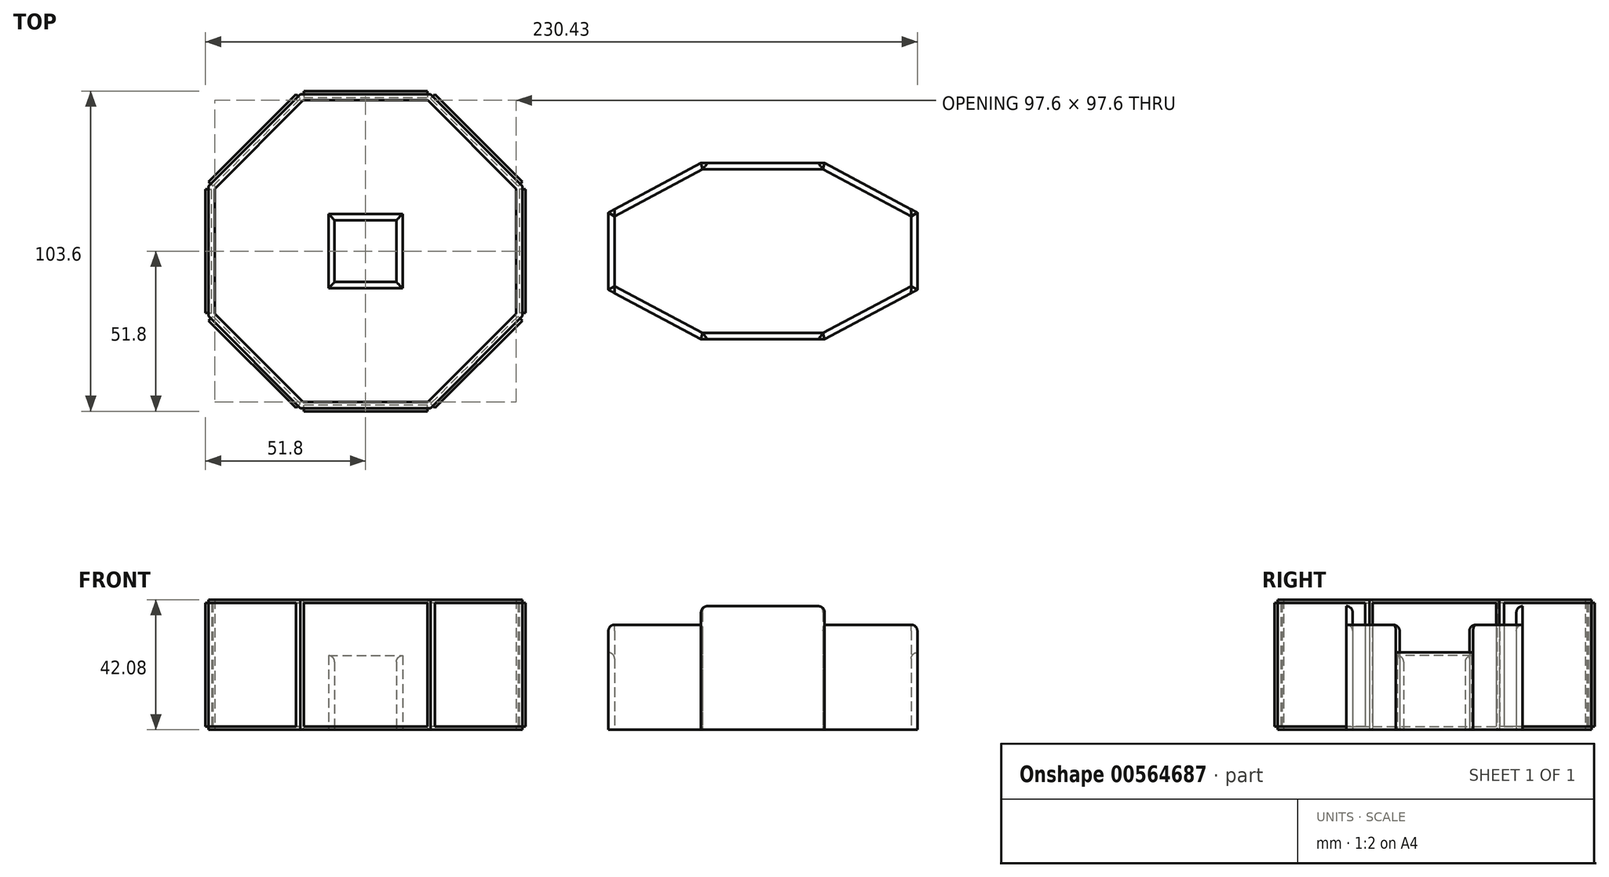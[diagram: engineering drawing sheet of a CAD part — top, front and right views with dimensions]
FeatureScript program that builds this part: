
annotation { "Feature Type Name" : "Feature", "Feature Type Description" : "" }
export const myFeature = defineFeature(function(context is Context, id is Id, definition is map)
    precondition{}
    {
        {
            var Q0;
            Q0=qCreatedBy(makeId("Top.planeOp"),FACE);
            var sketch = newSketch(context, id + "F0", { "sketchPlane" : qUnion([Q0])});
            skCircle(sketch, "E0.cCircle", {"center": v(0, 0) * mm, "radius": 50.8 * mm, "construction": true});
            skLineSegment(sketch, "E0.0", {"start": v(-50.8, -21.04) * mm, "end": v(-50.8, 21.04) * mm});
            skLineSegment(sketch, "E0.1", {"start": v(-50.8, 21.04) * mm, "end": v(-21.04, 50.8) * mm});
            skLineSegment(sketch, "E0.2", {"start": v(-21.04, 50.8) * mm, "end": v(21.04, 50.8) * mm});
            skLineSegment(sketch, "E0.3", {"start": v(21.04, 50.8) * mm, "end": v(50.8, 21.04) * mm});
            skLineSegment(sketch, "E0.4", {"start": v(50.8, 21.04) * mm, "end": v(50.8, -21.04) * mm});
            skLineSegment(sketch, "E0.5", {"start": v(50.8, -21.04) * mm, "end": v(21.04, -50.8) * mm});
            skLineSegment(sketch, "E0.6", {"start": v(21.04, -50.8) * mm, "end": v(-21.04, -50.8) * mm});
            skLineSegment(sketch, "E0.7", {"start": v(-21.04, -50.8) * mm, "end": v(-50.8, -21.04) * mm});
            skPoint(sketch, "E0.0.midPoint", {"position": v(-50.8, 0) * mm});
            skLineSegment(sketch, "E1.0", {"start": v(-48.8, -20.21) * mm, "end": v(-48.8, 20.21) * mm});
            skLineSegment(sketch, "E1.1", {"start": v(-20.21, -48.8) * mm, "end": v(-48.8, -20.21) * mm});
            skLineSegment(sketch, "E1.2", {"start": v(-48.8, 20.21) * mm, "end": v(-20.21, 48.8) * mm});
            skLineSegment(sketch, "E1.3", {"start": v(20.21, -48.8) * mm, "end": v(-20.21, -48.8) * mm});
            skLineSegment(sketch, "E1.4", {"start": v(-20.21, 48.8) * mm, "end": v(20.21, 48.8) * mm});
            skLineSegment(sketch, "E1.5", {"start": v(20.21, 48.8) * mm, "end": v(48.8, 20.21) * mm});
            skLineSegment(sketch, "E1.6", {"start": v(48.8, 20.21) * mm, "end": v(48.8, -20.21) * mm});
            skLineSegment(sketch, "E1.7", {"start": v(48.8, -20.21) * mm, "end": v(20.21, -48.8) * mm});
            skSolve(sketch);
        }
        {
            var Q0;
            Q0 = qSketchRegion(id + "F0", true);
            extrude(context, id + "F1", {"entities" : qUnion([Q0]), "depth" : 42.08 * mm, "offsetDistance" : 25.4 * mm});
        }
        {
            var Q0;
            Q0=qCreatedBy(makeId("Top.planeOp"),FACE);
            var sketch = newSketch(context, id + "F2", { "sketchPlane" : qUnion([Q0])});
            skCircle(sketch, "E2.cCircle", {"center": v(0, 0) * mm, "radius": 12 * mm, "construction": true});
            skLineSegment(sketch, "E2.0", {"start": v(12, 12) * mm, "end": v(12, -12) * mm});
            skLineSegment(sketch, "E2.1", {"start": v(12, -12) * mm, "end": v(-12, -12) * mm});
            skLineSegment(sketch, "E2.2", {"start": v(-12, -12) * mm, "end": v(-12, 12) * mm});
            skLineSegment(sketch, "E2.3", {"start": v(-12, 12) * mm, "end": v(12, 12) * mm});
            skPoint(sketch, "E2.0.midPoint", {"position": v(12, 0) * mm});
            skLineSegment(sketch, "E3.0", {"start": v(10, -10) * mm, "end": v(-10, -10) * mm});
            skLineSegment(sketch, "E3.1", {"start": v(10, 10) * mm, "end": v(10, -10) * mm});
            skLineSegment(sketch, "E3.2", {"start": v(-10, 10) * mm, "end": v(10, 10) * mm});
            skLineSegment(sketch, "E3.3", {"start": v(-10, -10) * mm, "end": v(-10, 10) * mm});
            skSolve(sketch);
        }
        {
            var Q0;
            Q0 = qSketchRegion(id + "F2", true);
            extrude(context, id + "F3", {"entities" : qUnion([Q0]), "depth" : 24 * mm, "offsetDistance" : 25.4 * mm});
        }
        {
            var Q0;
            Q0=makeQuery(id+"F1.opExtrude","SWEPT_FACE",FACE,{"disambiguationData":[OSD([sQuery(id+"F0.wireOp",EDGE,"E0.2")])]});
            var sketch = newSketch(context, id + "F4", { "sketchPlane" : qUnion([Q0])});
            skLineSegment(sketch, "E4.bottom", {"start": v(20, 41.04) * mm, "end": v(-20, 41.04) * mm});
            skLineSegment(sketch, "E4.top", {"start": v(20, 1.04) * mm, "end": v(-20, 1.04) * mm});
            skLineSegment(sketch, "E4.left", {"start": v(20, 41.04) * mm, "end": v(20, 1.04) * mm});
            skLineSegment(sketch, "E4.right", {"start": v(-20, 41.04) * mm, "end": v(-20, 1.04) * mm});
            skPoint(sketch, "E4.middle", {"position": v(0, 21.04) * mm});
            skPoint(sketch, "E4.middle.positionSnap0", {"position": v(-21.04, 21.04) * mm});
            skPoint(sketch, "E4.middle.positionSnap1", {"position": v(0, 0) * mm});
            skPoint(sketch, "E4.centerSnap0", {"position": v(-21.04, 21.04) * mm});
            skPoint(sketch, "E4.centerSnap1", {"position": v(0, 0) * mm});
            skSolve(sketch);
        }
        {
            var Q0;
            Q0 = qSketchRegion(id + "F4", true);
            extrude(context, id + "F5", {"entities" : qUnion([Q0]), "endBound" : BoundingType.SYMMETRIC, "depth" : 2 * mm, "offsetDistance" : 25.4 * mm});
        }
        {
            var Q0;
            Q0=qCreatedBy(makeId("Front.planeOp"),FACE);
            var sketch = newSketch(context, id + "F6", { "sketchPlane" : qUnion([Q0])});
            skLineSegment(sketch, "E5", {"start": v(0, 0) * mm, "end": v(0, 64.3) * mm});
            skSolve(sketch);
        }
        {
            var Q0;
            Q0=makeQuery(id+"F5.opExtrude","SWEPT_BODY",BODY,{"disambiguationData":[OSD([sQuery(id+"F4.wireOp",EDGE,"E4.bottom"),sQuery(id+"F4.wireOp",EDGE,"E4.top"),sQuery(id+"F4.wireOp",EDGE,"E4.left"),sQuery(id+"F4.wireOp",EDGE,"E4.right")])]});
            var Q1;
            Q1=sQuery(id+"F6.wireOp",EDGE,"E5");
            circularPattern(context, id + "F7", {"entities" : qUnion([Q0]), "axis" : qUnion([Q1]), "angle" : 360 * degree, "instanceCount" : 8, "equalSpace" : true});
        }
        {
            var Q0;
            Q0=qCreatedBy(makeId("Top.planeOp"),FACE);
            var sketch = newSketch(context, id + "F8", { "sketchPlane" : qUnion([Q0])});
            skLineSegment(sketch, "E6", {"start": v(78.63, 0) * mm, "end": v(78.63, 12.5) * mm});
            skLineSegment(sketch, "E7", {"start": v(78.63, 12.5) * mm, "end": v(108.63, 28.5) * mm});
            skLineSegment(sketch, "E8", {"start": v(108.63, 28.5) * mm, "end": v(148.63, 28.5) * mm});
            skLineSegment(sketch, "E9", {"start": v(148.63, 28.5) * mm, "end": v(178.63, 12.5) * mm});
            skLineSegment(sketch, "E10", {"start": v(178.63, 12.5) * mm, "end": v(178.63, 0) * mm});
            skLineSegment(sketch, "E11", {"start": v(78.63, 0) * mm, "end": v(178.63, 0) * mm, "construction": true});
            skLineSegment(sketch, "E12.MirrorCS", {"start": v(178.63, -12.5) * mm, "end": v(178.63, 0) * mm});
            skLineSegment(sketch, "E13.MirrorCS", {"start": v(148.63, -28.5) * mm, "end": v(178.63, -12.5) * mm});
            skLineSegment(sketch, "E14.MirrorCS", {"start": v(108.63, -28.5) * mm, "end": v(148.63, -28.5) * mm});
            skLineSegment(sketch, "E15.MirrorCS", {"start": v(78.63, 0) * mm, "end": v(78.63, -12.5) * mm});
            skLineSegment(sketch, "E16.MirrorCS", {"start": v(78.63, -12.5) * mm, "end": v(108.63, -28.5) * mm});
            skLineSegment(sketch, "E17.0", {"start": v(80.63, 11.3) * mm, "end": v(109.13, 26.5) * mm});
            skLineSegment(sketch, "E17.1", {"start": v(80.63, 0) * mm, "end": v(80.63, 11.3) * mm});
            skLineSegment(sketch, "E17.2", {"start": v(109.13, 26.5) * mm, "end": v(148.13, 26.5) * mm});
            skLineSegment(sketch, "E17.3", {"start": v(80.63, 0) * mm, "end": v(80.63, -11.3) * mm});
            skLineSegment(sketch, "E17.4", {"start": v(80.63, -11.3) * mm, "end": v(109.13, -26.5) * mm});
            skLineSegment(sketch, "E17.5", {"start": v(109.13, -26.5) * mm, "end": v(148.13, -26.5) * mm});
            skLineSegment(sketch, "E17.6", {"start": v(148.13, 26.5) * mm, "end": v(176.63, 11.3) * mm});
            skLineSegment(sketch, "E17.7", {"start": v(176.63, 11.3) * mm, "end": v(176.63, 0) * mm});
            skLineSegment(sketch, "E17.8", {"start": v(176.63, -11.3) * mm, "end": v(176.63, 0) * mm});
            skLineSegment(sketch, "E17.9", {"start": v(148.13, -26.5) * mm, "end": v(176.63, -11.3) * mm});
            skLineSegment(sketch, "E18", {"start": v(109.13, -26.5) * mm, "end": v(108.63, -28.5) * mm});
            skLineSegment(sketch, "E19", {"start": v(148.13, -26.5) * mm, "end": v(148.63, -28.5) * mm});
            skLineSegment(sketch, "E20", {"start": v(80.63, -11.3) * mm, "end": v(78.63, -12.5) * mm});
            skLineSegment(sketch, "E21", {"start": v(80.63, 11.3) * mm, "end": v(78.63, 12.5) * mm});
            skLineSegment(sketch, "E22", {"start": v(109.13, 26.5) * mm, "end": v(108.63, 28.5) * mm});
            skLineSegment(sketch, "E23", {"start": v(148.13, 26.5) * mm, "end": v(148.63, 28.5) * mm});
            skLineSegment(sketch, "E24", {"start": v(176.63, 11.3) * mm, "end": v(178.63, 12.5) * mm});
            skLineSegment(sketch, "E25", {"start": v(178.63, -12.5) * mm, "end": v(176.63, -11.3) * mm});
            skSolve(sketch);
        }
        {
            var Q0;
            Q0=makeQuery(id+"F8.imprint","IMPRINT",FACE,{"disambiguationData":[TD([[makeQuery(id+"F8.imprint","IMPRINT",EDGE,{"derivedFrom":sQuery(id+"F8.wireOp",EDGE,"E6")}),-1.0]])]});
            var Q1;
            Q1=makeQuery(id+"F8.imprint","IMPRINT",FACE,{"disambiguationData":[TD([[makeQuery(id+"F8.imprint","IMPRINT",EDGE,{"derivedFrom":sQuery(id+"F8.wireOp",EDGE,"E10")}),-1.0]])]});
            extrude(context, id + "F9", {"entities" : qUnion([Q0, Q1]), "depth" : 25 * mm, "offsetDistance" : 25 * mm});
        }
        {
            var Q0;
            Q0=makeQuery(id+"F8.imprint","IMPRINT",FACE,{"disambiguationData":[TD([[makeQuery(id+"F8.imprint","IMPRINT",EDGE,{"derivedFrom":sQuery(id+"F8.wireOp",EDGE,"E8")}),-1.0]])]});
            var Q1;
            Q1=makeQuery(id+"F8.imprint","IMPRINT",FACE,{"disambiguationData":[TD([[makeQuery(id+"F8.imprint","IMPRINT",EDGE,{"derivedFrom":sQuery(id+"F8.wireOp",EDGE,"E14.MirrorCS")}),1.0]])]});
            var Q2;
            Q2=sQuery(id+"F8.wireOp",EDGE,"E17.5");
            var Q3;
            Q3=sQuery(id+"F8.wireOp",EDGE,"E14.MirrorCS");
            var Q4;
            Q4=sQuery(id+"F8.wireOp",EDGE,"E18");
            var Q5;
            Q5=sQuery(id+"F8.wireOp",EDGE,"E19");
            var Q6;
            Q6=sQuery(id+"F8.wireOp",EDGE,"E23");
            var Q7;
            Q7=sQuery(id+"F8.wireOp",EDGE,"E8");
            var Q8;
            Q8=sQuery(id+"F8.wireOp",EDGE,"E17.2");
            var Q9;
            Q9=sQuery(id+"F8.wireOp",EDGE,"E22");
            extrude(context, id + "F10", {"entities" : qUnion([Q0, Q1]), "surfaceEntities" : qUnion([Q2, Q3, Q4, Q5, Q6, Q7, Q8, Q9]), "depth" : 40 * mm, "offsetDistance" : 25 * mm});
        }
        {
            var Q0;
            Q0=makeQuery(id+"F8.imprint","IMPRINT",FACE,{"disambiguationData":[TD([[makeQuery(id+"F8.imprint","IMPRINT",EDGE,{"derivedFrom":sQuery(id+"F8.wireOp",EDGE,"E13.MirrorCS")}),1.0]])]});
            var Q1;
            Q1=makeQuery(id+"F8.imprint","IMPRINT",FACE,{"disambiguationData":[TD([[makeQuery(id+"F8.imprint","IMPRINT",EDGE,{"derivedFrom":sQuery(id+"F8.wireOp",EDGE,"E16.MirrorCS")}),1.0]])]});
            var Q2;
            Q2=makeQuery(id+"F8.imprint","IMPRINT",FACE,{"disambiguationData":[TD([[makeQuery(id+"F8.imprint","IMPRINT",EDGE,{"derivedFrom":sQuery(id+"F8.wireOp",EDGE,"E7")}),-1.0]])]});
            var Q3;
            Q3=makeQuery(id+"F8.imprint","IMPRINT",FACE,{"disambiguationData":[TD([[makeQuery(id+"F8.imprint","IMPRINT",EDGE,{"derivedFrom":sQuery(id+"F8.wireOp",EDGE,"E9")}),-1.0]])]});
            extrude(context, id + "F11", {"entities" : qUnion([Q0, Q1, Q2, Q3]), "depth" : 34 * mm, "offsetDistance" : 25 * mm});
        }
        {
            var Q0;
            Q0=makeQuery(id+"F9.opExtrude","CAP_EDGE",EDGE,{"disambiguationData":[OSD([sQuery(id+"F8.wireOp",EDGE,"E17.1"),sQuery(id+"F8.wireOp",EDGE,"E17.3")])],"isStart":false});
            var Q1;
            Q1=makeQuery(id+"F11.opExtrude","CAP_EDGE",EDGE,{"disambiguationData":[OSD([sQuery(id+"F8.wireOp",EDGE,"E17.4")])],"isStart":false});
            var Q2;
            Q2=makeQuery(id+"F10.opExtrude","CAP_EDGE",EDGE,{"disambiguationData":[OSD([sQuery(id+"F8.wireOp",EDGE,"E17.2")])],"isStart":false});
            var Q3;
            Q3=makeQuery(id+"F11.opExtrude","CAP_EDGE",EDGE,{"disambiguationData":[OSD([sQuery(id+"F8.wireOp",EDGE,"E17.6")])],"isStart":false});
            var Q4;
            Q4=makeQuery(id+"F9.opExtrude","CAP_EDGE",EDGE,{"disambiguationData":[OSD([sQuery(id+"F8.wireOp",EDGE,"E17.7"),sQuery(id+"F8.wireOp",EDGE,"E17.8")])],"isStart":false});
            var Q5;
            Q5=makeQuery(id+"F11.opExtrude","CAP_EDGE",EDGE,{"disambiguationData":[OSD([sQuery(id+"F8.wireOp",EDGE,"E17.9")])],"isStart":false});
            var Q6;
            Q6=makeQuery(id+"F10.opExtrude","CAP_EDGE",EDGE,{"disambiguationData":[OSD([sQuery(id+"F8.wireOp",EDGE,"E17.5")])],"isStart":false});
            var Q7;
            Q7=makeQuery(id+"F11.opExtrude","CAP_EDGE",EDGE,{"disambiguationData":[OSD([sQuery(id+"F8.wireOp",EDGE,"E17.0")])],"isStart":false});
            var Q8;
            Q8=makeQuery(id+"F11.opExtrude","CAP_EDGE",EDGE,{"disambiguationData":[OSD([sQuery(id+"F8.wireOp",EDGE,"E21")])],"isStart":false});
            var Q9;
            Q9=makeQuery(id+"F10.opExtrude","CAP_EDGE",EDGE,{"disambiguationData":[OSD([sQuery(id+"F8.wireOp",EDGE,"E22")])],"isStart":false});
            var Q10;
            Q10=makeQuery(id+"F10.opExtrude","CAP_EDGE",EDGE,{"disambiguationData":[OSD([sQuery(id+"F8.wireOp",EDGE,"E23")])],"isStart":false});
            var Q11;
            Q11=makeQuery(id+"F11.opExtrude","CAP_EDGE",EDGE,{"disambiguationData":[OSD([sQuery(id+"F8.wireOp",EDGE,"E24")])],"isStart":false});
            var Q12;
            Q12=makeQuery(id+"F11.opExtrude","CAP_EDGE",EDGE,{"disambiguationData":[OSD([sQuery(id+"F8.wireOp",EDGE,"E25")])],"isStart":false});
            var Q13;
            Q13=makeQuery(id+"F10.opExtrude","CAP_EDGE",EDGE,{"disambiguationData":[OSD([sQuery(id+"F8.wireOp",EDGE,"E19")])],"isStart":false});
            var Q14;
            Q14=makeQuery(id+"F10.opExtrude","CAP_EDGE",EDGE,{"disambiguationData":[OSD([sQuery(id+"F8.wireOp",EDGE,"E18")])],"isStart":false});
            var Q15;
            Q15=makeQuery(id+"F11.opExtrude","CAP_EDGE",EDGE,{"disambiguationData":[OSD([sQuery(id+"F8.wireOp",EDGE,"E20")])],"isStart":false});
            fillet(context, id + "F12", {"entities" : qUnion([Q0, Q1, Q2, Q3, Q4, Q5, Q6, Q7, Q8, Q9, Q10, Q11, Q12, Q13, Q14, Q15]), "radius" : 2 * mm, "tangentPropagation" : true, "allowEdgeOverflow" : false});
        }
        {
            var Q0;
            Q0=makeQuery(id+"F3.opExtrude","CAP_EDGE",EDGE,{"disambiguationData":[OSD([sQuery(id+"F2.wireOp",EDGE,"E3.2")])],"isStart":false});
            var Q1;
            Q1=makeQuery(id+"F3.opExtrude","CAP_EDGE",EDGE,{"disambiguationData":[OSD([sQuery(id+"F2.wireOp",EDGE,"E3.3")])],"isStart":false});
            var Q2;
            Q2=makeQuery(id+"F3.opExtrude","CAP_EDGE",EDGE,{"disambiguationData":[OSD([sQuery(id+"F2.wireOp",EDGE,"E3.1")])],"isStart":false});
            var Q3;
            Q3=makeQuery(id+"F3.opExtrude","CAP_EDGE",EDGE,{"disambiguationData":[OSD([sQuery(id+"F2.wireOp",EDGE,"E3.0")])],"isStart":false});
            fillet(context, id + "F13", {"entities" : qUnion([Q0, Q1, Q2, Q3]), "radius" : 2 * mm, "tangentPropagation" : true, "allowEdgeOverflow" : false});
        }
    });
